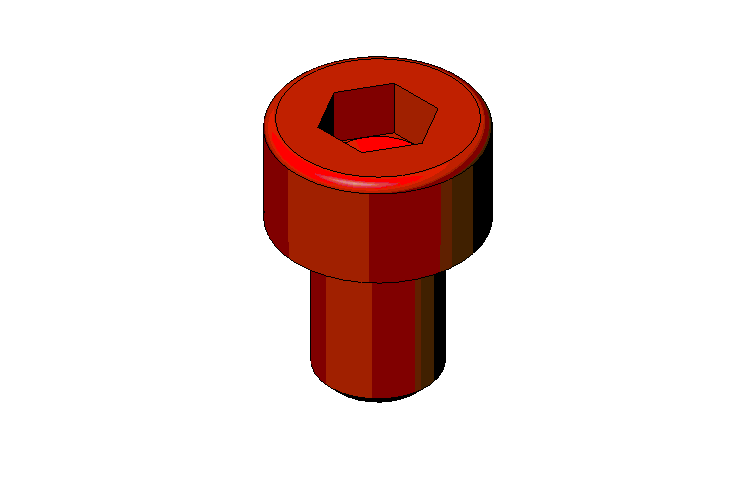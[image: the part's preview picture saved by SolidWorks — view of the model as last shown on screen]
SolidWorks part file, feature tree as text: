
SOLIDWORKS PART (.sldprt)
format: sldprt  version: not decoded by parser v0  size: 226,304 bytes
history: native  units: mm
features: plane x3, sketch x3, material x1, extrude x1, chamfer x1, revolve x1, cut_extrude x1 (+10 scaffold rows collapsed)
feature tree (21):
  scaffold x10  (default folders/planes/origin — collapsed)
  material  "Matériau <non spécifié>"
  plane  "Plan1"
  plane  "Plan2"
  plane  "Plan3"
  sketch  "Esquisse2"  dims[Diamètre nominal=5.0mm]
  extrude  "Base-Extrusion"  Depth=7mm Longueur sous tête=7mm
  chamfer  "Chanfrein1"  Distance=0.5mm Angle=45deg
  sketch  "Esquisse5"  dims[c1.D2=0.45mm c1.Hauteur tête=2.0mm c1.Cote sur plats=5.5mm c1.D3=~2.780036mm c2.D3=30.0deg c2.D4=2.75mm c2.Diamètre tête=8.5mm c2.Diamètre nominal=3.0mm c2.D1=4.25mm c3.D3=3.0mm c4.D3=60.0deg c4.Diamètre nominal=4.5mm c4.Cote sur plats=4.0mm c4.D4=2.25mm c4.D5=2.0mm]
  revolve  "Boss.-Révol.1"  Angle=360deg
  sketch  "Esquisse7"  dims[c1.D1=~2.410714mm c2.D1=30.0deg c2.D2=~1.370242mm c3.D2=30.0deg c3.D3=2.5mm]
  cut_extrude  "Enlèv. mat.-Extru.1"  Depth=2.25mm
decode coverage: 7 of 7 modeling features carry decoded parameters
note: ~ marks probable driven/reference dimensions
note: suppression state not decoded; provenance and decode notes live in map.json
